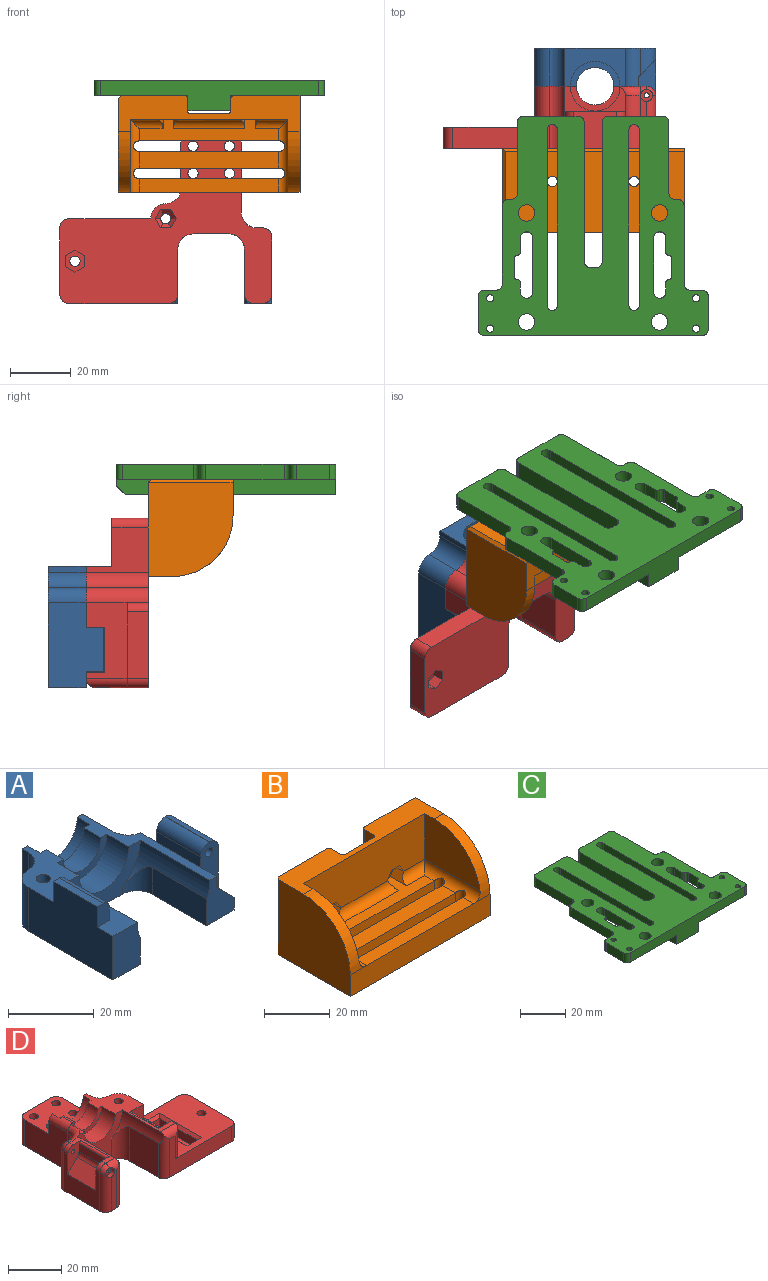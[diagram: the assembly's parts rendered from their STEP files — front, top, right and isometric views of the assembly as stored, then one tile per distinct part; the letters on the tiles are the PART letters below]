
ASSEMBLY  parts=4 mates=3
PART A: 45 faces, bbox 40x40x18.3 mm
  f0: cylinder r=1.7mm len=6.5mm, axis (0,0,-1), area 69.4mm2, adj f2,f37
  f1: plane 12.5x2mm, normal (-1,0,0), area 25mm2, adj f2,f11,f12,f43
  f2: plane 40x13.8mm, normal (0,0,1), area 258.3mm2, adj f0,f1,f6,f7,f8,f9,f11,f13
  f3: plane 40x8mm, normal (0,0,1), area 106.1mm2, adj f4,f7,f10,f11,f13,f14,f15,f16
  f4: plane 12.5x9mm, normal (0,-1,0), area 75.1mm2, adj f3,f5,f12,f18,f19,f31,f39
  f5: plane 20x15.5mm, normal (1,0,0), area 246.3mm2, adj f4,f12,f23,f24,f27,f39,f40,f42
  f6: cylinder r=12mm len=23mm, axis (0,1,0), area 123.5mm2, adj f2,f7,f8,f20,f21
  f7: plane 24x12.5mm, normal (0,-1,0), area 132.8mm2, adj f2,f3,f6,f12,f17,f18,f21,f22
  f8: plane 12.5x9mm, normal (0,-1,0), area 109.3mm2, adj f2,f6,f9,f12,f20
  f9: plane 28x18.3mm, normal (-1,0,0), area 434.7mm2, adj f2,f8,f12,f32,f34,f35,f44
  f10: plane 12.5x10mm, normal (1,0,0), area 125mm2, adj f3,f11,f12,f41
  f11: plane 20x12.5mm, normal (0,1,0), area 144.4mm2, adj f1,f2,f3,f10,f12,f16
  f12: plane 40x40mm, normal (0,0,-1), area 856.5mm2, adj f1,f4,f5,f7,f8,f9,f10,f11
  f13: plane 16.4x8.2mm, normal (0,1,0), area 45.2mm2, adj f2,f3,f15,f16
  f14: plane 16.4x8.2mm, normal (0,-1,0), area 45.2mm2, adj f2,f3,f15,f17
  f15: cylinder r=6.2mm len=12.4mm, axis (0,-1,0), area 109.1mm2, adj f2,f3,f13,f14
  f16: cylinder r=8.2mm len=16.4mm, axis (0,-1,0), area 108.2mm2, adj f2,f3,f11,f13
  f17: cylinder r=8.2mm len=16.4mm, axis (0,-1,0), area 185.5mm2, adj f2,f3,f7,f14
  f18: cylinder r=12mm len=23mm, axis (0,1,0), area 123.5mm2, adj f3,f4,f7,f19,f22
  f19: plane 18x7.7mm, normal (-1,0,0), area 138.7mm2, adj f4,f12,f18,f22
  f20: plane 18x7.7mm, normal (1,0,0), area 138.7mm2, adj f6,f8,f12,f21
  f21: cylinder r=5mm len=7.7mm, axis (0,0,1), area 40.5mm2, adj f6,f7,f12,f20
  f22: cylinder r=5mm len=7.7mm, axis (0,0,-1), area 40.5mm2, adj f7,f12,f18,f19
  f23: plane 14.6x5.8mm, normal (0,-1,0), area 60mm2, adj f5,f25,f26,f27,f28,f29,f31,f39
  f24: plane 14.6x5.8mm, normal (0,1,0), area 60mm2, adj f5,f25,f26,f27,f28,f29,f30,f40
  f25: plane 14.6x3mm, normal (-1,0,0), area 43.8mm2, adj f3,f23,f24,f28
  f26: plane 14.6x0.2mm, normal (0,0,1), area 2.9mm2, adj f23,f24,f27,f28
  f27: cylinder r=2.8mm len=14.6mm, axis (0,-1,0), area 64.2mm2, adj f5,f23,f24,f26
  f28: cylinder r=2.8mm len=14.6mm, axis (0,1,0), area 64.2mm2, adj f23,f24,f25,f26
  f29: cylinder r=1.2mm len=14.6mm, axis (0,1,0), area 110.1mm2, adj f23,f24
  f30: plane 5.26x3mm, normal (1,0,0), area 15.8mm2, adj f3,f24,f40,f41
  f31: plane 5.2x3mm, normal (1,0,0), area 15.6mm2, adj f3,f4,f23,f39
  f32: plane 5.8x4mm, normal (0,-1,0), area 22.3mm2, adj f2,f9,f33,f35,f36
  f33: plane 14.6x3.8mm, normal (1,0,0), area 55.5mm2, adj f2,f32,f34,f36
  f34: plane 5.8x4mm, normal (0,1,0), area 22.3mm2, adj f2,f9,f33,f35,f36
  f35: plane 14.6x2mm, normal (0,0,1), area 29.2mm2, adj f9,f32,f34,f36
  f36: cylinder r=2mm len=14.6mm, axis (0,-1,0), area 45.9mm2, adj f32,f33,f34,f35
  f37: plane 6x6mm, normal (0,0,-1), area 19.2mm2, adj f0,f38
  f38: cylinder r=3mm len=6mm, axis (0,0,-1), area 113.1mm2, adj f12,f37
  f39: plane 5.8x5.8mm, normal (0.71,0,0.71), area 42.7mm2, adj f4,f5,f23,f31
  f40: plane 5.8x5.8mm, normal (0.71,0,0.71), area 35.1mm2, adj f5,f24,f30,f41,f42
  f41: cylinder r=5mm len=12.5mm, axis (0,0,-1), area 95.4mm2, adj f3,f10,f12,f30,f40,f42
  f42: cylinder r=5mm len=8.7mm, axis (0,0,1), area 43.3mm2, adj f5,f12,f40,f41
  f43: cylinder r=5mm len=12.5mm, axis (0,0,-1), area 98.2mm2, adj f1,f2,f12,f44
  f44: cylinder r=5mm len=12.5mm, axis (0,0,1), area 98.2mm2, adj f2,f9,f12,f43
PART B: 59 faces, bbox 60x32x28 mm
  f0: plane 46x4.6mm, normal (0,0,1), area 211.6mm2, adj f8,f27,f52,f56
  f1: plane 46x5.6mm, normal (0,0,1), area 257.6mm2, adj f28,f29,f52,f56
  f2: plane 27x21.8mm, normal (0,1,0), area 579.5mm2, adj f3,f9,f25,f38,f51
  f3: plane 60x12mm, normal (0,0,1), area 425.1mm2, adj f2,f6,f7,f9,f10,f11,f12,f35
  f4: plane 46x11mm, normal (0,0,1), area 232.5mm2, adj f13,f14,f16,f19,f20,f21,f30,f52
  f5: plane 60x31mm, normal (0,0,-1), area 1428.3mm2, adj f8,f9,f10,f27,f28,f29,f30,f31
  f6: plane 27x20.8mm, normal (0,1,0), area 552.5mm2, adj f3,f26,f39,f42,f43
  f7: plane 52x17mm, normal (0,-1,0), area 852.8mm2, adj f3,f11,f12,f15,f17,f18,f22,f23
  f8: plane 60x8mm, normal (0,-1,0), area 480mm2, adj f0,f5,f9,f10,f57,f58
  f9: plane 32x28mm, normal (1,0,0), area 809.7mm2, adj f2,f3,f5,f8,f51,f57
  f10: plane 31x28mm, normal (-1,0,0), area 782.2mm2, adj f3,f5,f8,f42,f58
  f11: plane 23.77x17mm, normal (1,0,0), area 322.4mm2, adj f3,f7,f52,f58
  f12: plane 23.77x17mm, normal (-1,0,0), area 322.4mm2, adj f3,f7,f56,f57
  f13: plane 6.93x6mm, normal (0,-1,0), area 22.1mm2, adj f4,f14,f15,f16,f17,f18,f26
  f14: plane 7x3mm, normal (-0.87,0,0.5), area 16.1mm2, adj f4,f13,f15,f54
  f15: plane 4x3mm, normal (-0.87,0,-0.5), area 13.9mm2, adj f7,f13,f14,f17
  f16: plane 7x3mm, normal (0.87,0,0.5), area 16.1mm2, adj f4,f13,f18,f53
  f17: plane 4x3.46mm, normal (0,0,-1), area 13.9mm2, adj f7,f13,f15,f18
  f18: plane 4x3mm, normal (0.87,0,-0.5), area 13.9mm2, adj f7,f13,f16,f17
  f19: plane 6.93x6mm, normal (0,-1,0), area 22.1mm2, adj f4,f20,f21,f22,f23,f24,f25
  f20: plane 7x3mm, normal (0.87,0,0.5), area 16.1mm2, adj f4,f19,f24,f54
  f21: plane 7x3mm, normal (-0.87,0,0.5), area 16.1mm2, adj f4,f19,f22,f55
  f22: plane 4x3mm, normal (-0.87,0,-0.5), area 13.9mm2, adj f7,f19,f21,f23
  f23: plane 4x3.46mm, normal (0,0,-1), area 13.9mm2, adj f7,f19,f22,f24
  f24: plane 4x3mm, normal (0.87,0,-0.5), area 13.9mm2, adj f7,f19,f20,f23
  f25: cylinder r=1.7mm len=4mm, axis (0,-1,0), area 42.7mm2, adj f2,f19
  f26: cylinder r=1.7mm len=4mm, axis (0,-1,0), area 42.7mm2, adj f6,f13
  f27: plane 46.6x8.02mm, normal (0,1,0), area 372.8mm2, adj f0,f5,f31,f32,f52,f56
  f28: plane 46.6x8.02mm, normal (0,-1,0), area 372.8mm2, adj f1,f5,f31,f32,f52,f56
  f29: plane 46.6x8.02mm, normal (0,1,0), area 372.8mm2, adj f1,f5,f33,f34,f52,f56
  f30: plane 46.6x8.02mm, normal (0,-1,0), area 372.8mm2, adj f4,f5,f33,f34,f52,f56
  f31: cylinder r=1.7mm len=8.76mm, axis (0,0,1), area 44.9mm2, adj f5,f27,f28,f56
  f32: cylinder r=1.7mm len=8.76mm, axis (0,0,-1), area 44.9mm2, adj f5,f27,f28,f52
  f33: cylinder r=1.7mm len=8.76mm, axis (0,0,-1), area 44.9mm2, adj f5,f29,f30,f56
  f34: cylinder r=1.7mm len=8.76mm, axis (0,0,1), area 44.9mm2, adj f5,f29,f30,f52
  f35: plane 27x4mm, normal (1,0,0), area 108mm2, adj f3,f39,f41,f45
  f36: plane 27x4mm, normal (-1,0,0), area 108mm2, adj f3,f38,f40,f49
  f37: plane 27x12.4mm, normal (0,1,0), area 334.8mm2, adj f3,f40,f41,f47
  f38: cylinder r=1mm len=27mm, axis (0,0,-1), area 42.4mm2, adj f2,f3,f36,f50
  f39: cylinder r=1mm len=27mm, axis (0,0,1), area 42.4mm2, adj f3,f6,f35,f44
  f40: cylinder r=1mm len=27mm, axis (0,0,-1), area 42.4mm2, adj f3,f36,f37,f48
  f41: cylinder r=1mm len=27mm, axis (0,0,1), area 42.4mm2, adj f3,f35,f37,f46
  f42: plane 28x1mm, normal (-0.71,0.71,0), area 38.9mm2, adj f3,f6,f10,f43
  f43: plane 21.8x1mm, normal (0,0.71,-0.71), area 30.1mm2, adj f5,f6,f42,f44
  f44: cone r=1mm half-angle=45deg, axis (0,0,1), area 1.1mm2, adj f39,f43,f45
  f45: plane 4x1mm, normal (0.71,0,-0.71), area 5.7mm2, adj f5,f35,f44,f46
  f46: cone r=2mm half-angle=45deg, axis (0,0,-1), area 3.3mm2, adj f5,f41,f45,f47
  f47: plane 12.4x1mm, normal (0,0.71,-0.71), area 17.5mm2, adj f5,f37,f46,f48
  f48: cone r=2mm half-angle=45deg, axis (0,0,-1), area 3.3mm2, adj f5,f40,f47,f49
  f49: plane 4x1mm, normal (-0.71,0,-0.71), area 5.7mm2, adj f5,f36,f48,f50
  f50: cone r=1mm half-angle=45deg, axis (0,0,1), area 1.1mm2, adj f38,f49,f51
  f51: plane 21.8x1mm, normal (0,0.71,-0.71), area 30.8mm2, adj f2,f5,f9,f50
  f52: cylinder r=3mm len=24mm, axis (0,1,0), area 95.8mm2, adj f0,f1,f4,f11,f27,f28,f29,f30
  f53: cylinder r=3mm len=10.77mm, axis (1,0,0), area 42.6mm2, adj f4,f7,f16,f52
  f54: cylinder r=3mm len=23.54mm, axis (1,0,0), area 105mm2, adj f4,f7,f14,f20
  f55: cylinder r=3mm len=10.77mm, axis (1,0,0), area 42.6mm2, adj f4,f7,f21,f56
  f56: cylinder r=3mm len=24mm, axis (0,-1,0), area 95.8mm2, adj f0,f1,f4,f12,f27,f28,f29,f30
  f57: cylinder r=20mm len=20mm, axis (-1,0,0), area 127.6mm2, adj f3,f8,f9,f12,f56
  f58: cylinder r=20mm len=20mm, axis (-1,0,0), area 127.6mm2, adj f3,f8,f10,f11,f52
PART C: 76 faces, bbox 76x72.5x10 mm
  f0: plane 72.5x31mm, normal (0,0,-1), area 1286.6mm2, adj f3,f4,f9,f10,f11,f12,f13,f14
  f1: plane 5x3.2mm, normal (-1,0,0), area 16mm2, adj f2,f5,f46,f66
  f2: plane 76x72.5mm, normal (0,0,1), area 3288.2mm2, adj f1,f3,f4,f6,f7,f8,f9,f10
  f3: plane 5x3.2mm, normal (1,0,0), area 16mm2, adj f0,f2,f48,f68
  f4: plane 18x7mm, normal (0,1,0), area 94mm2, adj f0,f2,f42,f56,f71,f75
  f5: plane 72.5x31mm, normal (0,0,-1), area 1286.6mm2, adj f1,f6,f7,f8,f14,f15,f16,f17
  f6: plane 5x1mm, normal (0,1,0), area 5mm2, adj f2,f5,f49,f54
  f7: plane 23.5x5mm, normal (1,0,0), area 117.5mm2, adj f2,f5,f49,f55
  f8: plane 18x7mm, normal (0,1,0), area 94mm2, adj f2,f5,f41,f55,f72,f74
  f9: plane 23.5x5mm, normal (-1,0,0), area 117.5mm2, adj f0,f2,f50,f56
  f10: plane 5x1mm, normal (0,1,0), area 5mm2, adj f0,f2,f50,f51
  f11: plane 26x5mm, normal (-1,0,0), area 130mm2, adj f0,f2,f51,f52
  f12: plane 5x4mm, normal (0,1,0), area 20mm2, adj f0,f2,f52,f57
  f13: plane 11x5mm, normal (-1,0,0), area 55mm2, adj f0,f2,f57,f58
  f14: plane 72x10mm, normal (0,-1,0), area 430mm2, adj f0,f2,f5,f58,f59,f71,f72,f73
  f15: plane 11x5mm, normal (1,0,0), area 55mm2, adj f2,f5,f59,f60
  f16: plane 5x4mm, normal (0,1,0), area 20mm2, adj f2,f5,f53,f60
  f17: plane 26x5mm, normal (1,0,0), area 130mm2, adj f2,f5,f53,f54
  f18: cylinder r=2.7mm len=5.4mm, axis (0,0,1), area 84.8mm2, adj f0,f2
  f19: plane 5x4.8mm, normal (1,0,0), area 24mm2, adj f0,f2,f47,f70
  f20: plane 18x5mm, normal (-1,0,0), area 90mm2, adj f0,f2,f47,f48
  f21: plane 5x4.8mm, normal (-1,0,0), area 24mm2, adj f2,f5,f45,f64
  f22: plane 18x5mm, normal (1,0,0), area 90mm2, adj f2,f5,f45,f46
  f23: cylinder r=1.7mm len=5mm, axis (0,0,1), area 26.7mm2, adj f2,f5,f24,f25
  f24: plane 58x5mm, normal (1,0,0), area 290mm2, adj f2,f5,f23,f26
  f25: plane 58x5mm, normal (-1,0,0), area 290mm2, adj f2,f5,f23,f26
  f26: cylinder r=1.7mm len=5mm, axis (0,0,1), area 26.7mm2, adj f2,f5,f24,f25
  f27: plane 46x10mm, normal (-1,0,0), area 459.5mm2, adj f2,f41,f43,f73,f74
  f28: plane 46x10mm, normal (1,0,0), area 459.5mm2, adj f2,f42,f44,f73,f75
  f29: plane 10x2mm, normal (0,1,0), area 20mm2, adj f2,f43,f44,f73
  f30: plane 58x5mm, normal (1,0,0), area 290mm2, adj f0,f2,f31,f33
  f31: cylinder r=1.7mm len=5mm, axis (0,0,1), area 26.7mm2, adj f0,f2,f30,f32
  f32: plane 58x5mm, normal (-1,0,0), area 290mm2, adj f0,f2,f31,f33
  f33: cylinder r=1.7mm len=5mm, axis (0,0,1), area 26.7mm2, adj f0,f2,f30,f32
  f34: cylinder r=2.7mm len=5.4mm, axis (0,0,1), area 84.8mm2, adj f2,f5
  f35: cylinder r=2.7mm len=5.4mm, axis (0,0,1), area 84.8mm2, adj f2,f5
  f36: cylinder r=2.7mm len=5.4mm, axis (0,0,1), area 84.8mm2, adj f0,f2
  f37: cylinder r=1.2mm len=5mm, axis (0,0,1), area 37.7mm2, adj f0,f2
  f38: cylinder r=1.2mm len=5mm, axis (0,0,1), area 37.7mm2, adj f0,f2
  f39: cylinder r=1.2mm len=5mm, axis (0,0,1), area 37.7mm2, adj f2,f5
  f40: cylinder r=1.2mm len=5mm, axis (0,0,1), area 37.7mm2, adj f2,f5
  f41: cylinder r=2mm len=9mm, axis (0,0,-1), area 24.3mm2, adj f2,f8,f27,f74
  f42: cylinder r=2mm len=9mm, axis (0,0,1), area 24.3mm2, adj f2,f4,f28,f75
  f43: cylinder r=2mm len=10mm, axis (0,0,-1), area 31.4mm2, adj f2,f27,f29,f73
  f44: cylinder r=2mm len=10mm, axis (0,0,1), area 31.4mm2, adj f2,f28,f29,f73
  f45: cylinder r=2mm len=5mm, axis (0,0,-1), area 31.4mm2, adj f2,f5,f21,f22
  f46: cylinder r=2mm len=5mm, axis (0,0,1), area 31.4mm2, adj f1,f2,f5,f22
  f47: cylinder r=2mm len=5mm, axis (0,0,-1), area 31.4mm2, adj f0,f2,f19,f20
  f48: cylinder r=2mm len=5mm, axis (0,0,1), area 31.4mm2, adj f0,f2,f3,f20
  f49: cylinder r=2mm len=5mm, axis (0,0,-1), area 15.7mm2, adj f2,f5,f6,f7
  f50: cylinder r=2mm len=5mm, axis (0,0,1), area 15.7mm2, adj f0,f2,f9,f10
  f51: cylinder r=2mm len=5mm, axis (0,0,1), area 15.7mm2, adj f0,f2,f10,f11
  f52: cylinder r=2mm len=5mm, axis (0,0,-1), area 15.7mm2, adj f0,f2,f11,f12
  f53: cylinder r=2mm len=5mm, axis (0,0,-1), area 15.7mm2, adj f2,f5,f16,f17
  f54: cylinder r=2mm len=5mm, axis (0,0,-1), area 15.7mm2, adj f2,f5,f6,f17
  f55: cylinder r=2mm len=5mm, axis (0,0,1), area 15.7mm2, adj f2,f5,f7,f8
  f56: cylinder r=2mm len=5mm, axis (0,0,-1), area 15.7mm2, adj f0,f2,f4,f9
  f57: cylinder r=2mm len=5mm, axis (0,0,1), area 15.7mm2, adj f0,f2,f12,f13
  f58: cylinder r=2mm len=5mm, axis (0,0,-1), area 15.7mm2, adj f0,f2,f13,f14
  f59: cylinder r=2mm len=5mm, axis (0,0,1), area 15.7mm2, adj f2,f5,f14,f15
  f60: cylinder r=2mm len=5mm, axis (0,0,1), area 15.7mm2, adj f2,f5,f15,f16
  f61: plane 6x5mm, normal (1,0,0), area 30mm2, adj f0,f2,f67,f69
  f62: plane 6x5mm, normal (-1,0,0), area 30mm2, adj f2,f5,f63,f65
  f63: cylinder r=1mm len=5mm, axis (0,0,-1), area 7.9mm2, adj f2,f5,f62,f64
  f64: cylinder r=1mm len=5mm, axis (0,0,1), area 7.9mm2, adj f2,f5,f21,f63
  f65: cylinder r=1mm len=5mm, axis (0,0,1), area 7.9mm2, adj f2,f5,f62,f66
  f66: cylinder r=1mm len=5mm, axis (0,0,-1), area 7.9mm2, adj f1,f2,f5,f65
  f67: cylinder r=1mm len=5mm, axis (0,0,-1), area 7.9mm2, adj f0,f2,f61,f68
  f68: cylinder r=1mm len=5mm, axis (0,0,-1), area 7.9mm2, adj f0,f2,f3,f67
  f69: cylinder r=1mm len=5mm, axis (0,0,1), area 7.9mm2, adj f0,f2,f61,f70
  f70: cylinder r=1mm len=5mm, axis (0,0,1), area 7.9mm2, adj f0,f2,f19,f69
  f71: plane 72.5x5mm, normal (-1,0,0), area 358mm2, adj f0,f4,f14,f73,f75
  f72: plane 72.5x5mm, normal (1,0,0), area 358mm2, adj f5,f8,f14,f73,f74
  f73: plane 69.5x14mm, normal (0,0,-1), area 692.7mm2, adj f14,f27,f28,f29,f43,f44,f71,f72
  f74: plane 4x3mm, normal (0,0.71,-0.71), area 15.8mm2, adj f8,f27,f41,f72,f73
  f75: plane 4x3mm, normal (0,0.71,-0.71), area 15.8mm2, adj f4,f28,f42,f71,f73
PART D: 103 faces, bbox 70x56x20.5 mm
  f0: plane 27x7mm, normal (0,1,0), area 189mm2, adj f55,f80,f84,f85
  f1: plane 33x17.5mm, normal (0,-1,0), area 262.5mm2, adj f79,f81,f82,f83,f84,f85
  f2: plane 5.6x0.8mm, normal (0,0,1), area 4.5mm2, adj f16,f17,f18,f74
  f3: plane 2.93x2.79mm, normal (0,0,1), area 3.4mm2, adj f10,f20,f73
  f4: plane 20.5x15mm, normal (1,0,0), area 197mm2, adj f5,f7,f14,f56,f60,f84
  f5: plane 37x13.8mm, normal (0,0,1), area 187.7mm2, adj f4,f6,f10,f14,f16,f17,f18,f19
  f6: plane 25x13.5mm, normal (1,0,0), area 247.5mm2, adj f5,f38,f39,f41,f55,f81,f85
  f7: plane 20x16mm, normal (0,0,1), area 279.8mm2, adj f4,f14,f15,f24,f25,f26,f27,f28
  f8: cylinder r=12mm len=22.2mm, axis (0,1,0), area 116.9mm2, adj f9,f10,f23,f57,f73,f76,f78
  f9: plane 19.58x5mm, normal (0,0,1), area 35.6mm2, adj f8,f29,f31,f62,f63,f65,f72,f73
  f10: plane 24.03x20.53mm, normal (0,-1,0), area 228.8mm2, adj f3,f5,f8,f20,f21,f57,f58,f73
  f11: plane 17.5x3mm, normal (0,-1,0), area 49.4mm2, adj f33,f75,f76,f78,f84
  f12: plane 17.5x2mm, normal (0,1,0), area 31.9mm2, adj f35,f59,f70,f84
  f13: plane 19x17.5mm, normal (-1,0,0), area 197.5mm2, adj f29,f31,f62,f63,f66,f70,f75,f84
  f14: plane 20x8.5mm, normal (0,1,0), area 62.5mm2, adj f4,f5,f7,f15,f19,f74
  f15: plane 23x17.5mm, normal (-1,0,0), area 331mm2, adj f7,f14,f59,f61,f74,f84
  f16: plane 16.4x8.2mm, normal (0,1,0), area 45.1mm2, adj f2,f5,f18,f19,f74
  f17: plane 16.4x8.2mm, normal (0,-1,0), area 45.1mm2, adj f2,f5,f18,f20,f74
  f18: cylinder r=6.2mm len=12.4mm, axis (0,-1,0), area 109.1mm2, adj f2,f5,f16,f17
  f19: cylinder r=8.2mm len=16.4mm, axis (0,-1,0), area 107.2mm2, adj f5,f14,f16,f74
  f20: cylinder r=8.2mm len=16.4mm, axis (0,-1,0), area 184.9mm2, adj f3,f5,f10,f17,f73,f74
  f21: cylinder r=12mm len=22.2mm, axis (0,1,0), area 116.9mm2, adj f5,f10,f22,f58,f82,f83
  f22: plane 15.7x15mm, normal (-1,0,0), area 235.6mm2, adj f21,f58,f83,f84
  f23: plane 15.7x15mm, normal (1,0,0), area 235.6mm2, adj f8,f57,f76,f84
  f24: plane 14x12mm, normal (0,1,0), area 168mm2, adj f7,f60,f61,f84
  f25: cylinder r=1.7mm len=12mm, axis (0,0,1), area 128.2mm2, adj f7,f84
  f26: cylinder r=1.7mm len=12mm, axis (0,0,1), area 128.2mm2, adj f7,f84
  f27: cylinder r=1.7mm len=12mm, axis (0,0,1), area 128.2mm2, adj f7,f84
  f28: cylinder r=1.7mm len=12mm, axis (0,0,1), area 128.2mm2, adj f7,f84
  f29: plane 12x7mm, normal (0,1,0), area 49.8mm2, adj f9,f13,f30,f37,f62,f65,f66,f68
  f30: plane 15x3.76mm, normal (-1,0,0), area 56.4mm2, adj f29,f31,f65,f68
  f31: plane 12x7mm, normal (0,-1,0), area 49.8mm2, adj f9,f13,f30,f36,f63,f65,f66,f68
  f32: plane 4x4mm, normal (0,-1,0), area 10.3mm2, adj f33,f37
  f33: cylinder r=2mm len=4mm, axis (0,-1,0), area 20.4mm2, adj f11,f32,f75,f77,f78
  f34: plane 4x4mm, normal (0,1,0), area 10.3mm2, adj f35,f36
  f35: cylinder r=2mm len=4mm, axis (0,1,0), area 20.4mm2, adj f12,f34,f70,f71,f72
  f36: cylinder r=0.85mm len=3mm, axis (0,-1,0), area 16mm2, adj f31,f34
  f37: cylinder r=0.85mm len=3mm, axis (0,-1,0), area 16mm2, adj f29,f32
  f38: plane 7x6mm, normal (0,1,0), area 34.3mm2, adj f5,f6,f40,f41,f64,f67
  f39: plane 7x6mm, normal (0,-1,0), area 34.3mm2, adj f5,f6,f40,f41,f64,f67
  f40: plane 15x2mm, normal (1,0,0), area 30mm2, adj f38,f39,f64,f67
  f41: plane 15x3mm, normal (0,0,1), area 45mm2, adj f6,f38,f39,f67
  f42: plane 14.5x3.46mm, normal (0,-1,0), area 50.2mm2, adj f43,f45,f50,f84
  f43: plane 14.5x3mm, normal (-0.87,-0.5,0), area 50.2mm2, adj f42,f44,f48,f84
  f44: plane 14.5x3mm, normal (-0.87,0.5,0), area 50.2mm2, adj f43,f46,f49,f84
  f45: plane 14.5x3mm, normal (0.87,-0.5,0), area 50.2mm2, adj f42,f47,f52,f84
  f46: plane 14.5x3.46mm, normal (0,1,0), area 50.2mm2, adj f44,f47,f51,f84
  f47: plane 14.5x3mm, normal (0.87,0.5,0), area 50.2mm2, adj f45,f46,f53,f84
  f48: plane 3x2.61mm, normal (-0.61,-0.35,-0.71), area 5.2mm2, adj f43,f49,f50,f54
  f49: plane 3x2.61mm, normal (-0.61,0.35,-0.71), area 5.2mm2, adj f44,f48,f51,f54
  f50: plane 3.46x1.53mm, normal (0,-0.71,-0.71), area 5.2mm2, adj f42,f48,f52,f54
  f51: plane 3.46x1.53mm, normal (0,0.71,-0.71), area 5.2mm2, adj f46,f49,f53,f54
  f52: plane 3x2.61mm, normal (0.61,-0.35,-0.71), area 5.2mm2, adj f45,f50,f53,f54
  f53: plane 3x2.61mm, normal (0.61,0.35,-0.71), area 5.2mm2, adj f47,f51,f52,f54
  f54: cylinder r=1.7mm len=4.7mm, axis (0,0,1), area 49.4mm2, adj f5,f48,f49,f50,f51,f52,f53
  f55: cylinder r=5mm len=20.5mm, axis (0,0,1), area 161mm2, adj f0,f5,f6,f56,f84
  f56: cylinder r=5mm len=20.5mm, axis (0,0,-1), area 161mm2, adj f4,f5,f55,f84
  f57: cylinder r=5mm len=15.7mm, axis (0,0,1), area 103.3mm2, adj f8,f10,f23,f84
  f58: cylinder r=5mm len=15.7mm, axis (0,0,-1), area 103.3mm2, adj f10,f21,f22,f84
  f59: cylinder r=5mm len=17.5mm, axis (0,0,-1), area 137.4mm2, adj f12,f15,f73,f84
  f60: cylinder r=3mm len=12mm, axis (0,0,-1), area 56.5mm2, adj f4,f7,f24,f84
  f61: cylinder r=3mm len=12mm, axis (0,0,1), area 56.5mm2, adj f7,f15,f24,f84
  f62: cylinder r=3mm len=3mm, axis (0,1,0), area 9.4mm2, adj f9,f13,f29,f77
  f63: cylinder r=3mm len=3mm, axis (0,1,0), area 9.4mm2, adj f9,f13,f31,f71
  f64: cylinder r=1mm len=15mm, axis (0,1,0), area 23.6mm2, adj f5,f38,f39,f40
  f65: cylinder r=1mm len=15mm, axis (0,-1,0), area 23.6mm2, adj f9,f29,f30,f31
  f66: plane 15x5.12mm, normal (-0.71,0,0.71), area 108.6mm2, adj f13,f29,f31,f68
  f67: cylinder r=3mm len=15mm, axis (0,-1,0), area 70.7mm2, adj f38,f39,f40,f41
  f68: cylinder r=3mm len=15mm, axis (0,1,0), area 35.3mm2, adj f29,f30,f31,f66
  f69: plane 22x7mm, normal (1,0,0), area 154mm2, adj f79,f80,f84,f85
  f70: cylinder r=3mm len=17.5mm, axis (0,0,1), area 79.1mm2, adj f12,f13,f35,f71,f84
  f71: sphere r=3mm, area 10.5mm2, adj f35,f63,f70,f72
  f72: cylinder r=3mm len=3mm, axis (1,0,0), area 6.1mm2, adj f9,f35,f71,f73
  f73: torus R=8mm, axis (0,0,1), area 41.4mm2, adj f3,f8,f9,f10,f20,f59,f72,f74
  f74: cylinder r=3mm len=10mm, axis (0,1,0), area 41.7mm2, adj f2,f14,f15,f16,f17,f19,f20,f73
  f75: cylinder r=3mm len=17.5mm, axis (0,0,1), area 79.1mm2, adj f11,f13,f33,f77,f84
  f76: cylinder r=3mm len=19.54mm, axis (0,0,1), area 82.8mm2, adj f8,f11,f23,f78,f84
  f77: sphere r=3mm, area 10.5mm2, adj f33,f62,f75,f78
  f78: cylinder r=3mm len=5.04mm, axis (-1,0,0), area 18.2mm2, adj f8,f9,f11,f33,f76,f77
  f79: cylinder r=3mm len=7mm, axis (0,0,-1), area 33mm2, adj f1,f69,f84,f85
  f80: cylinder r=3mm len=7mm, axis (0,0,-1), area 33mm2, adj f0,f69,f84,f85
  f81: cylinder r=3mm len=13.5mm, axis (0,0,-1), area 58.5mm2, adj f1,f6,f82,f85
  f82: cylinder r=3mm len=8.04mm, axis (-1,0,0), area 30.5mm2, adj f1,f5,f21,f81,f83
  f83: cylinder r=3mm len=19.54mm, axis (0,0,-1), area 82.8mm2, adj f1,f21,f22,f82,f84
  f84: plane 70x56mm, normal (0,0,-1), area 1932.8mm2, adj f0,f1,f4,f10,f11,f12,f13,f15
  f85: plane 33x28mm, normal (0,0,1), area 654.3mm2, adj f0,f1,f6,f69,f79,f80,f81,f93
  f86: plane 7.27x6.3mm, normal (0,0,-1), area 25.3mm2, adj f87,f88,f89,f90,f91,f92,f93
  f87: plane 4x3.64mm, normal (-1,0,0), area 14.5mm2, adj f84,f86,f88,f90
  f88: plane 4x3.15mm, normal (-0.5,0.87,0), area 14.5mm2, adj f84,f86,f87,f89
  f89: plane 4x3.15mm, normal (0.5,0.87,0), area 14.5mm2, adj f84,f86,f88,f91
  f90: plane 4x3.15mm, normal (-0.5,-0.87,0), area 14.5mm2, adj f84,f86,f87,f92
  f91: plane 4x3.64mm, normal (1,0,0), area 14.5mm2, adj f84,f86,f89,f92
  f92: plane 4x3.15mm, normal (0.5,-0.87,0), area 14.5mm2, adj f84,f86,f90,f91
  f93: cylinder r=1.7mm len=3.4mm, axis (0,0,-1), area 32mm2, adj f85,f86
  f94: plane 20x5.4mm, normal (0,0,1), area 108mm2, adj f95,f96,f97,f98
  f95: plane 20x3.8mm, normal (-1,0,0), area 76mm2, adj f94,f96,f97,f100
  f96: plane 5.4x3.8mm, normal (0,1,0), area 20.5mm2, adj f94,f95,f98,f102
  f97: plane 5.4x3.8mm, normal (0,-1,0), area 20.5mm2, adj f94,f95,f98,f99
  f98: plane 20x3.8mm, normal (1,0,0), area 76mm2, adj f94,f96,f97,f101
  f99: plane 7.8x1.2mm, normal (0,-0.71,0.71), area 11.2mm2, adj f85,f97,f100,f101
  f100: plane 22.4x1.2mm, normal (-0.71,0,0.71), area 36mm2, adj f85,f95,f99,f102
  f101: plane 22.4x1.2mm, normal (0.71,0,0.71), area 36mm2, adj f85,f98,f99,f102
  f102: plane 7.8x1.2mm, normal (0,0.71,0.71), area 11.2mm2, adj f85,f96,f100,f101
PLACE A rot(axis=(1,0,0),90deg) t=(27.18,50.08,-5.46)mm
PLACE B rot(axis=(1,0,0),90deg) t=(26.52,17.08,27.24)mm
PLACE C t=(26.52,-22.32,43.24)mm fixed
PLACE D rot(axis=(0,0.71,0.71),180deg) t=(27.18,25.08,-5.46)mm fixed
MATE planar B.f26 <-> C.f0  axis (0,0,1) through (13.02,6.08,43.24)mm
MATE revolute A.f28 <-> D.f33  axis (0,0,1) through (44.18,34.58,-5.66)mm
MATE planar D.f28 <-> B.f33  axis (0,-1,0) through (33.18,17.08,26.54)mm
